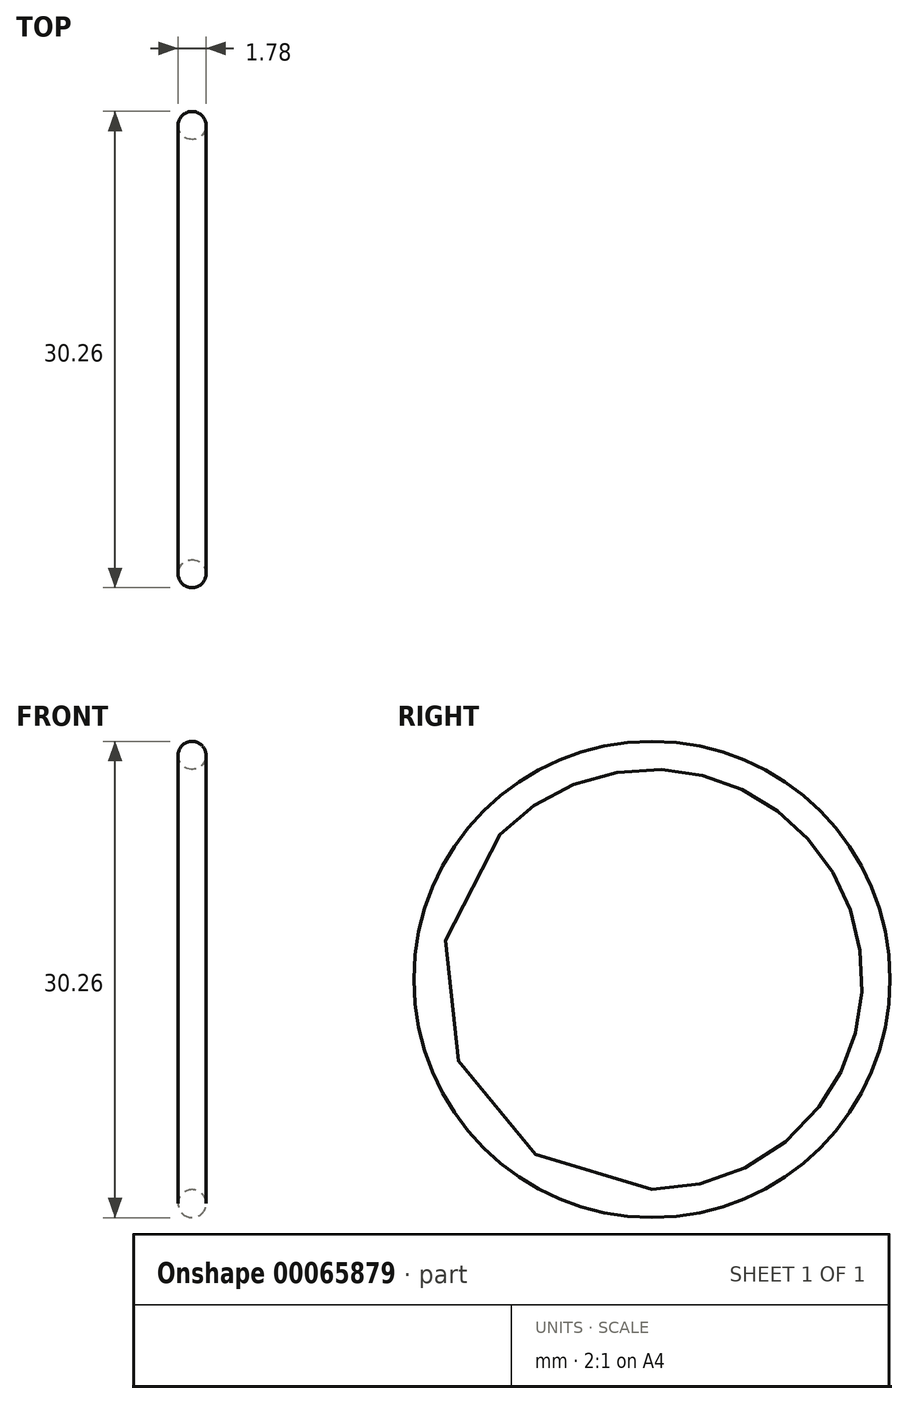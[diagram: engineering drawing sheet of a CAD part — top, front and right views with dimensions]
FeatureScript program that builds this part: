
annotation { "Feature Type Name" : "Feature", "Feature Type Description" : "" }
export const myFeature = defineFeature(function(context is Context, id is Id, definition is map)
    precondition{}
    {
        {
            var Q0;
            Q0=qCreatedBy(makeId("Front.planeOp"),FACE);
            var sketch = newSketch(context, id + "F0", { "sketchPlane" : qUnion([Q0])});
            skLineSegment(sketch, "E0", {"start": v(0, 0) * mm, "end": v(-6.06, 0) * mm, "construction": true});
            skCircle(sketch, "E1", {"center": v(0, 14.24) * mm, "radius": 0.89 * mm});
            skSolve(sketch);
        }
        {
            var Q0;
            Q0=makeQuery(id+"F0.imprint","IMPRINT",FACE,{"disambiguationData":[TD([[makeQuery(id+"F0.imprint","IMPRINT",EDGE,{"derivedFrom":sQuery(id+"F0.wireOp",EDGE,"E1")}),1.0]])]});
            var Q1;
            Q1=sQuery(id+"F0.wireOp",EDGE,"E0");
            revolve(context, id + "F1", {"entities" : qUnion([Q0]), "axis" : qUnion([Q1]), "revolveType" : RevolveType.FULL});
        }
    });
